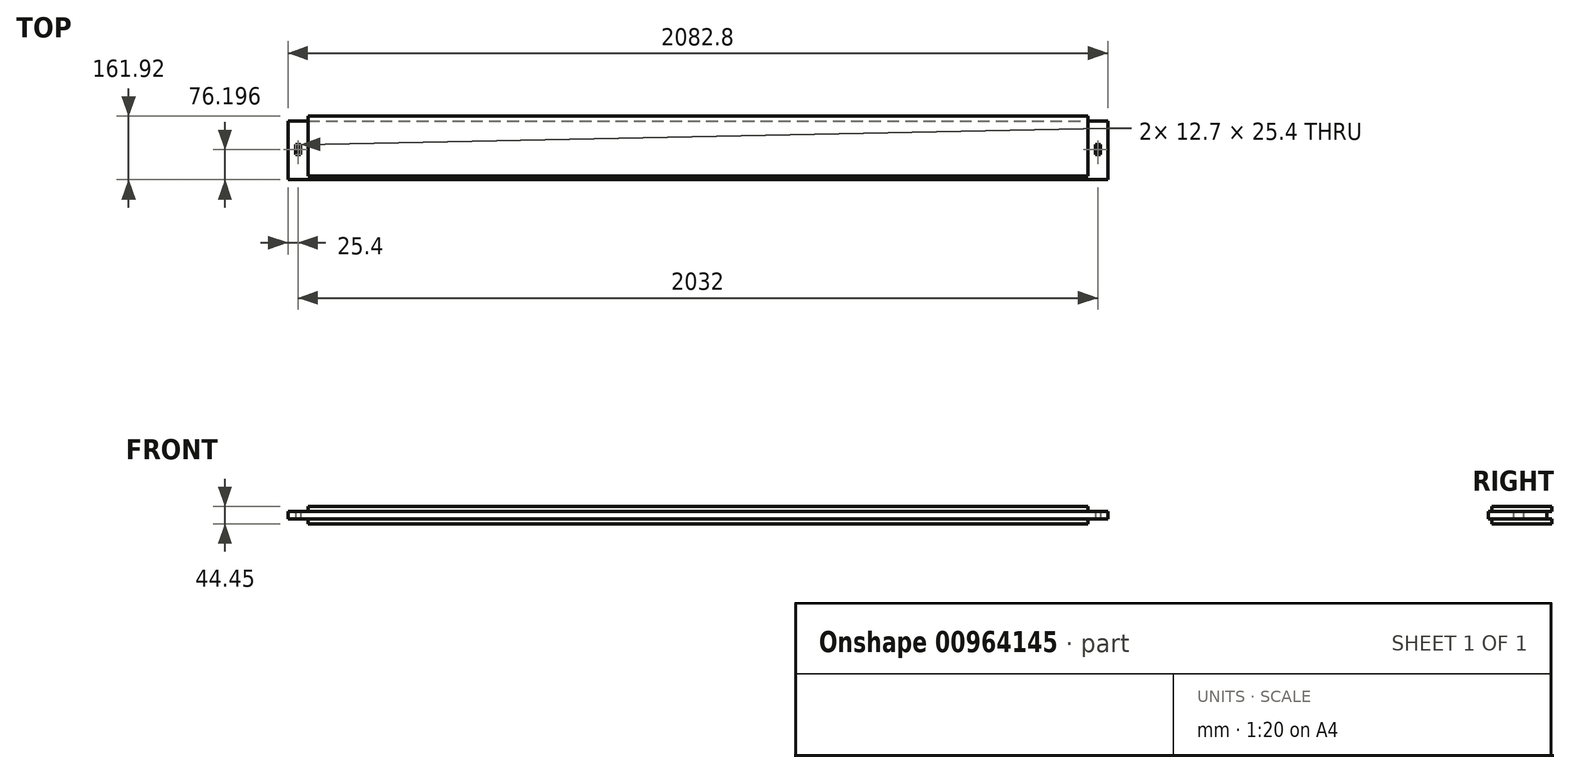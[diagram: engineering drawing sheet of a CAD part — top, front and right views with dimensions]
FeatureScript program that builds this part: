
annotation { "Feature Type Name" : "Feature", "Feature Type Description" : "" }
export const myFeature = defineFeature(function(context is Context, id is Id, definition is map)
    precondition{}
    {
        {
            var Q0;
            Q0=qCreatedBy(makeId("Top.planeOp"),FACE);
            var sketch = newSketch(context, id + "F0", { "sketchPlane" : qUnion([Q0])});
            skLineSegment(sketch, "E0.bottom", {"start": v(-960.45, -430.89) * mm, "end": v(1122.35, -430.89) * mm});
            skLineSegment(sketch, "E0.top", {"start": v(-960.45, -592.81) * mm, "end": v(1122.35, -592.81) * mm});
            skLineSegment(sketch, "E0.left", {"start": v(-960.45, -430.89) * mm, "end": v(-960.45, -592.81) * mm});
            skLineSegment(sketch, "E0.right", {"start": v(1122.35, -430.89) * mm, "end": v(1122.35, -592.81) * mm});
            skSolve(sketch);
        }
        {
            var Q0;
            Q0=qSketchRegion(id+"F0",true);
            extrude(context, id + "F1", {"entities" : qUnion([Q0]), "depth" : 44.45 * mm, "offsetDistance" : 25.4 * mm});
        }
        {
            var Q0;
            Q0=makeQuery(id+"F1.opExtrude","CAP_FACE",FACE,{"disambiguationData":[OSD([sQuery(id+"F0.wireOp",EDGE,"E0.bottom"),sQuery(id+"F0.wireOp",EDGE,"E0.top"),sQuery(id+"F0.wireOp",EDGE,"E0.left"),sQuery(id+"F0.wireOp",EDGE,"E0.right")])],"isStart":true});
            var sketch = newSketch(context, id + "F2", { "sketchPlane" : qUnion([Q0])});
            skLineSegment(sketch, "E1.bottom", {"start": v(-960.45, 430.89) * mm, "end": v(-909.65, 430.89) * mm});
            skLineSegment(sketch, "E1.top", {"start": v(-960.45, 592.81) * mm, "end": v(-909.65, 592.81) * mm});
            skLineSegment(sketch, "E1.left", {"start": v(-960.45, 592.81) * mm, "end": v(-960.45, 430.89) * mm});
            skLineSegment(sketch, "E1.right", {"start": v(-909.65, 592.81) * mm, "end": v(-909.65, 430.89) * mm});
            skLineSegment(sketch, "E2.bottom", {"start": v(1071.55, 430.89) * mm, "end": v(1122.35, 430.89) * mm});
            skLineSegment(sketch, "E2.top", {"start": v(1071.55, 592.81) * mm, "end": v(1122.35, 592.81) * mm});
            skLineSegment(sketch, "E2.left", {"start": v(1122.35, 592.81) * mm, "end": v(1122.35, 430.89) * mm});
            skLineSegment(sketch, "E2.right", {"start": v(1071.55, 592.81) * mm, "end": v(1071.55, 430.89) * mm});
            skLineSegment(sketch, "E3.bottom", {"start": v(-909.65, 592.81) * mm, "end": v(1071.55, 592.81) * mm});
            skLineSegment(sketch, "E3.top", {"start": v(-909.65, 583.29) * mm, "end": v(1071.55, 583.29) * mm});
            skLineSegment(sketch, "E3.left", {"start": v(-909.65, 592.81) * mm, "end": v(-909.65, 583.29) * mm});
            skLineSegment(sketch, "E3.right", {"start": v(1071.55, 592.81) * mm, "end": v(1071.55, 583.29) * mm});
            skSolve(sketch);
        }
        {
            var Q0;
            Q0=qSketchRegion(id+"F2",true);
            extrude(context, id + "F3", {"entities" : qUnion([Q0]), "operationType" : NewBodyOperationType.REMOVE, "oppositeDirection" : true, "depth" : 12.7 * mm, "offsetDistance" : 25.4 * mm});
        }
        {
            var Q0;
            Q0=makeQuery(id+"F1.opExtrude","CAP_FACE",FACE,{"disambiguationData":[OSD([sQuery(id+"F0.wireOp",EDGE,"E0.bottom"),sQuery(id+"F0.wireOp",EDGE,"E0.top"),sQuery(id+"F0.wireOp",EDGE,"E0.left"),sQuery(id+"F0.wireOp",EDGE,"E0.right"),sQuery(id+"F0.wireOp",EDGE,"qQXgVNNZ-AGSI-mXlc-8jnI-TWDtoKx84tdi.bottom"),sQuery(id+"F0.wireOp",EDGE,"qQXgVNNZ-AGSI-mXlc-8jnI-TWDtoKx84tdi.top"),sQuery(id+"F0.wireOp",EDGE,"qQXgVNNZ-AGSI-mXlc-8jnI-TWDtoKx84tdi.right"),sQuery(id+"F0.wireOp",EDGE,"eITyjntY-zXV5-UdZx-rjJQ-oeJIxLVityGO.bottom"),sQuery(id+"F0.wireOp",EDGE,"eITyjntY-zXV5-UdZx-rjJQ-oeJIxLVityGO.top"),sQuery(id+"F0.wireOp",EDGE,"eITyjntY-zXV5-UdZx-rjJQ-oeJIxLVityGO.right")])],"isStart":false});
            var sketch = newSketch(context, id + "F4", { "sketchPlane" : qUnion([Q0])});
            skLineSegment(sketch, "E4.bottom", {"start": v(-960.45, -430.89) * mm, "end": v(-960.45, -430.89) * mm});
            skLineSegment(sketch, "E5.bottom", {"start": v(1071.55, -430.89) * mm, "end": v(1122.35, -430.89) * mm});
            skLineSegment(sketch, "E5.top", {"start": v(1071.55, -592.81) * mm, "end": v(1122.35, -592.81) * mm});
            skLineSegment(sketch, "E5.left", {"start": v(1071.55, -430.89) * mm, "end": v(1071.55, -592.81) * mm});
            skLineSegment(sketch, "E5.right", {"start": v(1122.35, -430.89) * mm, "end": v(1122.35, -592.81) * mm});
            skLineSegment(sketch, "E6.bottom", {"start": v(-960.45, -592.81) * mm, "end": v(-909.65, -592.81) * mm});
            skLineSegment(sketch, "E6.top", {"start": v(-960.45, -430.89) * mm, "end": v(-909.65, -430.89) * mm});
            skLineSegment(sketch, "E6.left", {"start": v(-960.45, -592.81) * mm, "end": v(-960.45, -430.89) * mm});
            skLineSegment(sketch, "E6.right", {"start": v(-909.65, -592.81) * mm, "end": v(-909.65, -430.89) * mm});
            skLineSegment(sketch, "E7.bottom", {"start": v(-909.65, -592.81) * mm, "end": v(1071.55, -592.81) * mm});
            skLineSegment(sketch, "E7.top", {"start": v(-909.65, -583.29) * mm, "end": v(1071.55, -583.29) * mm});
            skLineSegment(sketch, "E7.left", {"start": v(-909.65, -592.81) * mm, "end": v(-909.65, -583.29) * mm});
            skLineSegment(sketch, "E7.right", {"start": v(1071.55, -592.81) * mm, "end": v(1071.55, -583.29) * mm});
            skSolve(sketch);
        }
        {
            var Q0;
            Q0=qSketchRegion(id+"F4",true);
            extrude(context, id + "F5", {"entities" : qUnion([Q0]), "operationType" : NewBodyOperationType.REMOVE, "oppositeDirection" : true, "depth" : 12.7 * mm, "offsetDistance" : 25.4 * mm});
        }
        {
            var Q0;
            Q0=makeQuery(id+"F1.opExtrude","SWEPT_FACE",FACE,{"disambiguationData":[OSD([sQuery(id+"F0.wireOp",EDGE,"E0.bottom")])]});
            var sketch = newSketch(context, id + "F6", { "sketchPlane" : qUnion([Q0])});
            skLineSegment(sketch, "E8.bottom", {"start": v(-1122.35, 31.75) * mm, "end": v(960.45, 31.75) * mm});
            skLineSegment(sketch, "E8.top", {"start": v(-1122.35, 12.7) * mm, "end": v(960.45, 12.7) * mm});
            skLineSegment(sketch, "E8.left", {"start": v(-1122.35, 31.75) * mm, "end": v(-1122.35, 12.7) * mm});
            skLineSegment(sketch, "E8.right", {"start": v(960.45, 31.75) * mm, "end": v(960.45, 12.7) * mm});
            skSolve(sketch);
        }
        {
            var Q0;
            Q0=qSketchRegion(id+"F6",true);
            extrude(context, id + "F7", {"entities" : qUnion([Q0]), "operationType" : NewBodyOperationType.REMOVE, "oppositeDirection" : true, "depth" : 12.7 * mm, "offsetDistance" : 25.4 * mm});
        }
        {
            var Q0;
            Q0=makeQuery(id+"F3.boolean.opBoolean","COPY",FACE,{"derivedFrom":makeQuery(id+"F3.opExtrude","CAP_FACE",FACE,{"disambiguationData":[OSD([sQuery(id+"F2.wireOp",EDGE,"E2.bottom"),sQuery(id+"F2.wireOp",EDGE,"E2.top"),sQuery(id+"F2.wireOp",EDGE,"E2.left"),sQuery(id+"F2.wireOp",EDGE,"E2.right")])],"isStart":false})});
            var sketch = newSketch(context, id + "F8", { "sketchPlane" : qUnion([Q0])});
            skLineSegment(sketch, "E9.bottom", {"start": v(-941.4, 503.91) * mm, "end": v(-928.7, 503.91) * mm});
            skLineSegment(sketch, "E9.top", {"start": v(-941.4, 529.31) * mm, "end": v(-928.7, 529.31) * mm});
            skLineSegment(sketch, "E9.left", {"start": v(-941.4, 503.91) * mm, "end": v(-941.4, 529.31) * mm});
            skLineSegment(sketch, "E9.right", {"start": v(-928.7, 503.91) * mm, "end": v(-928.7, 529.31) * mm});
            skLineSegment(sketch, "E10.bottom", {"start": v(1090.6, 503.91) * mm, "end": v(1103.3, 503.91) * mm});
            skLineSegment(sketch, "E10.top", {"start": v(1090.6, 529.31) * mm, "end": v(1103.3, 529.31) * mm});
            skLineSegment(sketch, "E10.left", {"start": v(1090.6, 503.91) * mm, "end": v(1090.6, 529.31) * mm});
            skLineSegment(sketch, "E10.right", {"start": v(1103.3, 503.91) * mm, "end": v(1103.3, 529.31) * mm});
            skSolve(sketch);
        }
        {
            var Q0;
            Q0=qSketchRegion(id+"F8",true);
            extrude(context, id + "F9", {"entities" : qUnion([Q0]), "operationType" : NewBodyOperationType.REMOVE, "endBound" : BoundingType.THROUGH_ALL, "oppositeDirection" : true, "depth" : 25.4 * mm, "offsetDistance" : 25.4 * mm});
        }
    });
